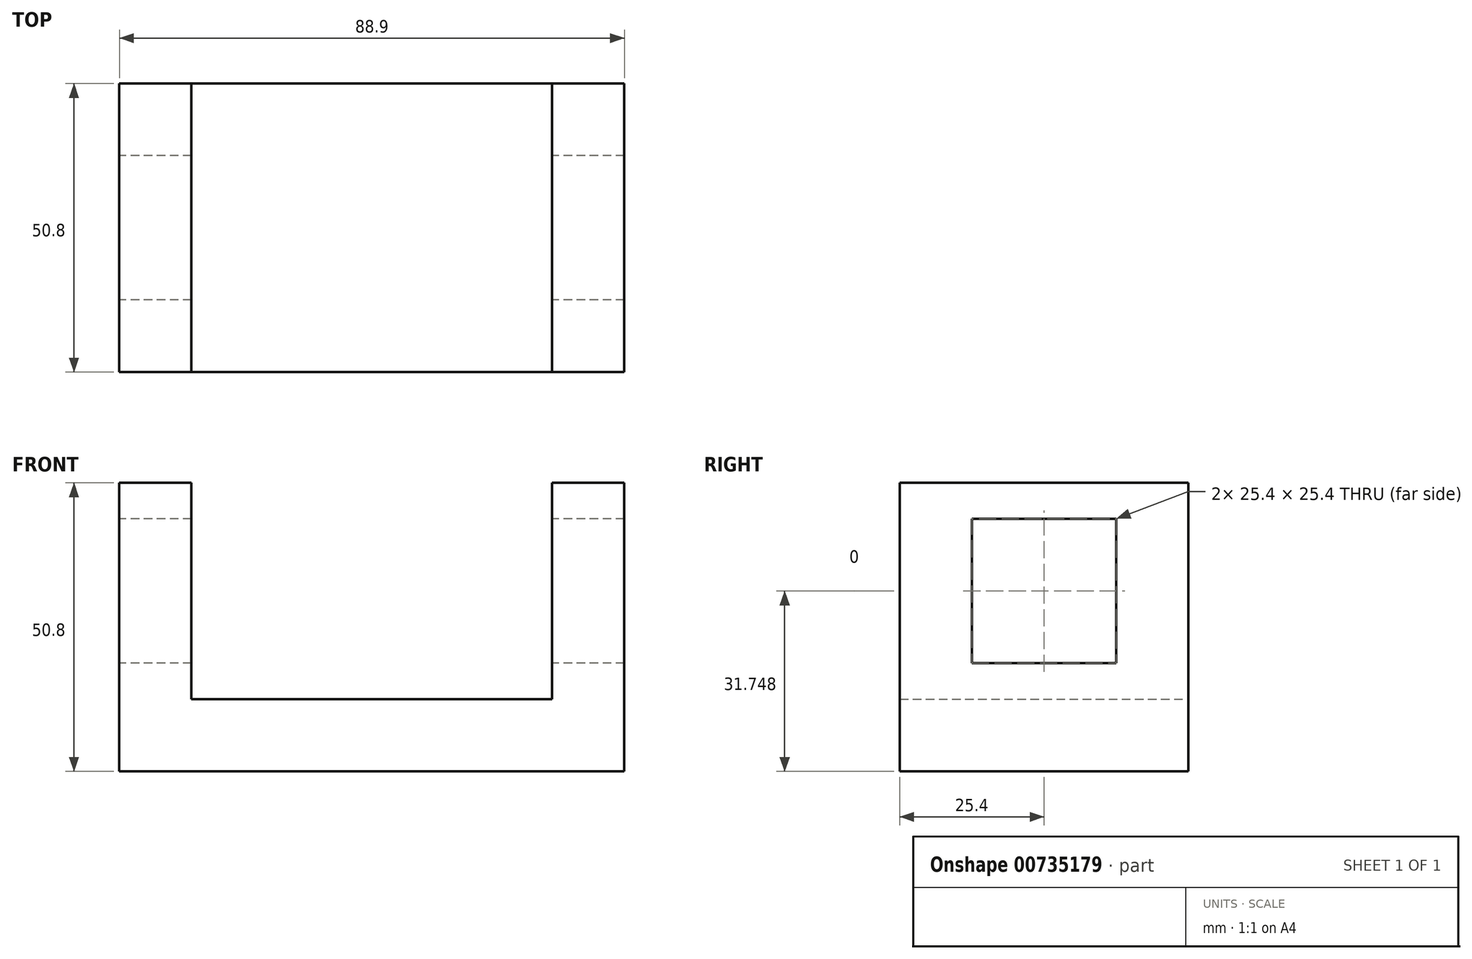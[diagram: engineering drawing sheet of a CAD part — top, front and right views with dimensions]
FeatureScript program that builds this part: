
annotation { "Feature Type Name" : "Feature", "Feature Type Description" : "" }
export const myFeature = defineFeature(function(context is Context, id is Id, definition is map)
    precondition{}
    {
        {
            var Q0;
            Q0=qCreatedBy(makeId("Front.planeOp"),FACE);
            var sketch = newSketch(context, id + "F0", { "sketchPlane" : qUnion([Q0])});
            skLineSegment(sketch, "E0", {"start": v(-45.7, 48.36) * mm, "end": v(-33, 48.36) * mm});
            skLineSegment(sketch, "E1", {"start": v(-45.7, 48.36) * mm, "end": v(-45.7, -2.44) * mm});
            skLineSegment(sketch, "E2", {"start": v(-45.7, -2.44) * mm, "end": v(43.2, -2.44) * mm});
            skLineSegment(sketch, "E3", {"start": v(43.2, -2.44) * mm, "end": v(43.2, 48.36) * mm});
            skLineSegment(sketch, "E4", {"start": v(43.2, 48.36) * mm, "end": v(30.5, 48.36) * mm});
            skLineSegment(sketch, "E5", {"start": v(-33, 48.36) * mm, "end": v(-33, 10.26) * mm});
            skLineSegment(sketch, "E6", {"start": v(30.5, 48.36) * mm, "end": v(30.5, 10.26) * mm});
            skLineSegment(sketch, "E7", {"start": v(30.5, 10.26) * mm, "end": v(-33, 10.26) * mm});
            skSolve(sketch);
        }
        {
            var Q0;
            Q0 = qSketchRegion(id + "F0", true);
            extrude(context, id + "F1", {"entities" : qUnion([Q0]), "depth" : 50.8 * mm, "offsetDistance" : 25.4 * mm});
        }
        {
            var Q0;
            Q0=makeQuery(id+"F1.opExtrude","SWEPT_FACE",FACE,{"disambiguationData":[OSD([sQuery(id+"F0.wireOp",EDGE,"E1")])]});
            var sketch = newSketch(context, id + "F2", { "sketchPlane" : qUnion([Q0])});
            skLineSegment(sketch, "E8.bottom", {"start": v(38.1, 42) * mm, "end": v(12.7, 42) * mm});
            skLineSegment(sketch, "E8.top", {"start": v(38.1, 16.6) * mm, "end": v(12.7, 16.6) * mm});
            skLineSegment(sketch, "E8.left", {"start": v(38.1, 42) * mm, "end": v(38.1, 16.6) * mm});
            skLineSegment(sketch, "E8.right", {"start": v(12.7, 42) * mm, "end": v(12.7, 16.6) * mm});
            skSolve(sketch);
        }
        {
            var Q0;
            Q0 = qSketchRegion(id + "F2", true);
            extrude(context, id + "F3", {"entities" : qUnion([Q0]), "operationType" : NewBodyOperationType.REMOVE, "oppositeDirection" : true, "depth" : 88.9 * mm, "offsetDistance" : 25.4 * mm});
        }
    });
